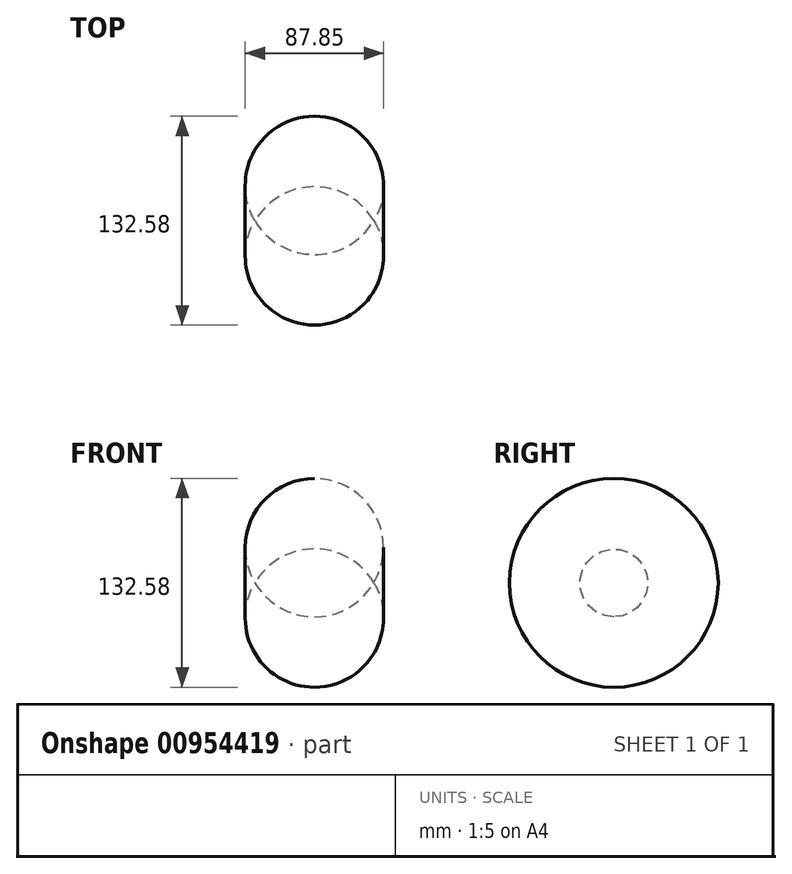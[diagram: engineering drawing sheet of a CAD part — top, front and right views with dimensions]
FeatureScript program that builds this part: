
annotation { "Feature Type Name" : "Feature", "Feature Type Description" : "" }
export const myFeature = defineFeature(function(context is Context, id is Id, definition is map)
    precondition{}
    {
        {
            var Q0;
            Q0=qCreatedBy(makeId("Front.planeOp"),FACE);
            var sketch = newSketch(context, id + "F0", { "sketchPlane" : qUnion([Q0])});
            skLineSegment(sketch, "E0", {"start": v(-75.6, 0) * mm, "end": v(0, 0) * mm});
            skArc(sketch, "E1", {"start": v(0, 0) * mm, "mid": v(-37.8, 21.56) * mm, "end": v(-75.6, 0) * mm});
            skSolve(sketch);
        }
        {
            var Q0;
            Q0=makeQuery(id+"F0.imprint","IMPRINT",FACE,{"disambiguationData":[TD([[makeQuery(id+"F0.imprint","IMPRINT",EDGE,{"derivedFrom":sQuery(id+"F0.wireOp",EDGE,"E0")}),1.0]])]});
            var Q1;
            Q1=sQuery(id+"F0.wireOp",EDGE,"E0");
            revolve(context, id + "F1", {"surfaceOperationType" : NewSurfaceOperationType.NEW, "entities" : qUnion([Q0]), "axis" : qUnion([Q1]), "revolveType" : RevolveType.FULL});
        }
    });
